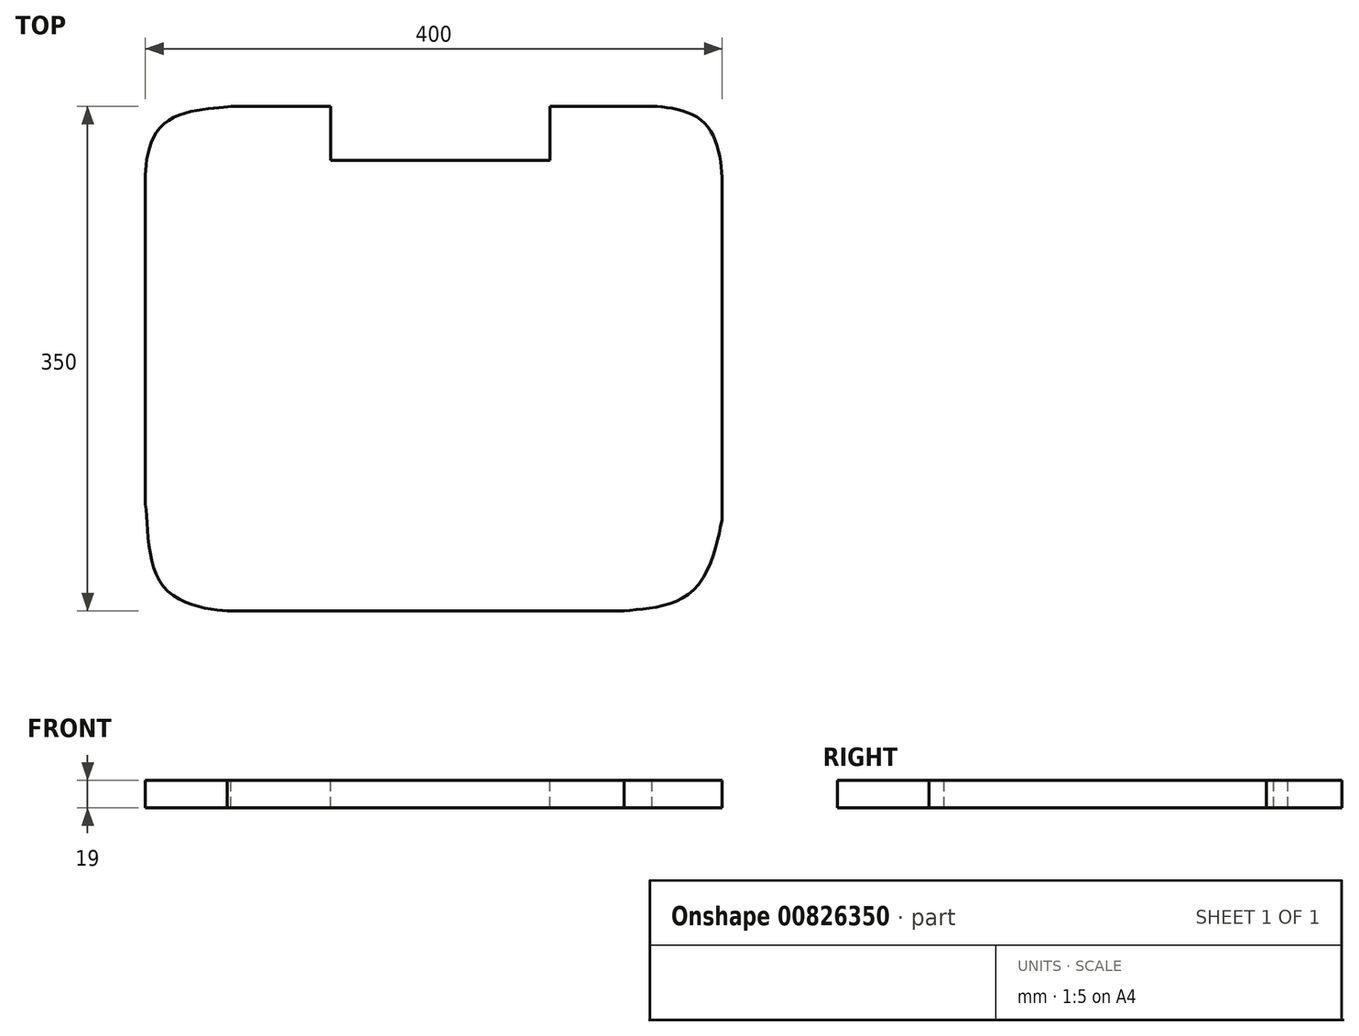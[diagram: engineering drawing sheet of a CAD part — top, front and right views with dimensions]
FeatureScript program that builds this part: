
annotation { "Feature Type Name" : "Feature", "Feature Type Description" : "" }
export const myFeature = defineFeature(function(context is Context, id is Id, definition is map)
    precondition{}
    {
        {
            var Q0;
            Q0=qCreatedBy(makeId("Top.planeOp"),FACE);
            var sketch = newSketch(context, id + "F0", { "sketchPlane" : qUnion([Q0])});
            skLineSegment(sketch, "E0.bottom", {"start": v(-200, 175) * mm, "end": v(200, 175) * mm});
            skLineSegment(sketch, "E0.top", {"start": v(-200, -175) * mm, "end": v(200, -175) * mm});
            skLineSegment(sketch, "E0.left", {"start": v(-200, 175) * mm, "end": v(-200, -175) * mm});
            skLineSegment(sketch, "E0.right", {"start": v(200, 175) * mm, "end": v(200, -175) * mm});
            skPoint(sketch, "E0.middle", {"position": v(0, 0) * mm});
            skSolve(sketch);
        }
        {
            var Q0;
            Q0=makeQuery(id+"F0.imprint","IMPRINT",FACE,{"disambiguationData":[TD([[makeQuery(id+"F0.imprint","IMPRINT",EDGE,{"derivedFrom":sQuery(id+"F0.wireOp",EDGE,"E0.bottom")}),-1.0]])]});
            extrude(context, id + "F1", {"entities" : qUnion([Q0]), "depth" : 19 * mm, "offsetDistance" : 25 * mm});
        }
        {
            var Q0;
            Q0=makeQuery(id+"F1.opExtrude","CAP_FACE",FACE,{"disambiguationData":[OSD([sQuery(id+"F0.wireOp",EDGE,"E0.bottom"),sQuery(id+"F0.wireOp",EDGE,"E0.top"),sQuery(id+"F0.wireOp",EDGE,"E0.left"),sQuery(id+"F0.wireOp",EDGE,"E0.right")])],"isStart":false});
            var sketch = newSketch(context, id + "F2", { "sketchPlane" : qUnion([Q0])});
            skFitSpline(sketch, "E1", {"points": [v(135.87, 175) * mm, v(187.94, 163.16) * mm, v(200, 110.13) * mm], "startDerivative": vector(58.12, 0) * mm, "endDerivative": vector(0, -51.3) * mm});
            skSolve(sketch);
        }
        {
            var Q0;
            {var subQ0=sQuery(id+"F2.wireOp",EDGE,"E1");var subQ1=makeQuery(id+"F1.opExtrude","CAP_EDGE",EDGE,{"disambiguationData":[OSD([sQuery(id+"F0.wireOp",EDGE,"E0.bottom")])],"isStart":false});var subQ2=makeQuery(id+"F2.imprint","INTERSECT",VERTEX,{"disambiguationData":[OD(1.0)],"derivedFrom":[subQ1,subQ0]});Q0=makeQuery(id+"F2.imprint","IMPRINT",FACE,{"disambiguationData":[TD([[makeQuery(id+"F2.imprint","IMPRINT",EDGE,{"disambiguationData":[TD([[subQ2,-1.0]])],"derivedFrom":subQ0}),1.0]])]});}
            extrude(context, id + "F3", {"entities" : qUnion([Q0]), "operationType" : NewBodyOperationType.REMOVE, "endBound" : BoundingType.THROUGH_ALL, "oppositeDirection" : true, "depth" : 31 * mm, "offsetDistance" : 25 * mm});
        }
        {
            var Q0;
            Q0=makeQuery(id+"F1.opExtrude","CAP_FACE",FACE,{"disambiguationData":[OSD([sQuery(id+"F0.wireOp",EDGE,"E0.bottom"),sQuery(id+"F0.wireOp",EDGE,"E0.top"),sQuery(id+"F0.wireOp",EDGE,"E0.left"),sQuery(id+"F0.wireOp",EDGE,"E0.right")])],"isStart":false});
            var sketch = newSketch(context, id + "F4", { "sketchPlane" : qUnion([Q0])});
            skFitSpline(sketch, "E2", {"points": [v(-140.76, 175) * mm, v(-189.63, 160.57) * mm, v(-200, 120.13) * mm, v(-200, 110.48) * mm], "startDerivative": vector(-65.65, -11.34) * mm, "endDerivative": vector(0, -155.76) * mm});
            skSolve(sketch);
        }
        {
            var Q0;
            {var subQ0=sQuery(id+"F4.wireOp",EDGE,"E2");var subQ1=makeQuery(id+"F1.opExtrude","CAP_EDGE",EDGE,{"disambiguationData":[OSD([sQuery(id+"F0.wireOp",EDGE,"E0.bottom")])],"isStart":false});var subQ2=makeQuery(id+"F4.imprint","INTERSECT",VERTEX,{"derivedFrom":[subQ1,subQ0]});Q0=makeQuery(id+"F4.imprint","IMPRINT",FACE,{"disambiguationData":[TD([[makeQuery(id+"F4.imprint","IMPRINT",EDGE,{"disambiguationData":[TD([[subQ2,-1.0]])],"derivedFrom":subQ0}),-1.0]])]});}
            extrude(context, id + "F5", {"entities" : qUnion([Q0]), "operationType" : NewBodyOperationType.REMOVE, "endBound" : BoundingType.THROUGH_ALL, "oppositeDirection" : true, "depth" : 25 * mm, "offsetDistance" : 25 * mm});
        }
        {
            var Q0;
            Q0=makeQuery(id+"F1.opExtrude","CAP_FACE",FACE,{"disambiguationData":[OSD([sQuery(id+"F0.wireOp",EDGE,"E0.bottom"),sQuery(id+"F0.wireOp",EDGE,"E0.top"),sQuery(id+"F0.wireOp",EDGE,"E0.left"),sQuery(id+"F0.wireOp",EDGE,"E0.right")])],"isStart":false});
            var sketch = newSketch(context, id + "F6", { "sketchPlane" : qUnion([Q0])});
            skFitSpline(sketch, "E3", {"points": [v(-200, -100.97) * mm, v(-187.15, -158.47) * mm, v(-143.25, -175) * mm, v(-132.74, -175) * mm], "startDerivative": vector(13.71, -104.16) * mm, "endDerivative": vector(42, 7.33) * mm});
            skSolve(sketch);
        }
        {
            var Q0;
            {var subQ0=sQuery(id+"F6.wireOp",EDGE,"E3");var subQ1=makeQuery(id+"F1.opExtrude","CAP_EDGE",EDGE,{"disambiguationData":[OSD([sQuery(id+"F0.wireOp",EDGE,"E0.left")])],"isStart":false});var subQ2=makeQuery(id+"F6.imprint","INTERSECT",VERTEX,{"derivedFrom":[subQ1,subQ0]});Q0=makeQuery(id+"F6.imprint","IMPRINT",FACE,{"disambiguationData":[TD([[makeQuery(id+"F6.imprint","IMPRINT",EDGE,{"disambiguationData":[TD([[subQ2,-1.0]])],"derivedFrom":subQ0}),-1.0]])]});}
            extrude(context, id + "F7", {"entities" : qUnion([Q0]), "operationType" : NewBodyOperationType.REMOVE, "endBound" : BoundingType.THROUGH_ALL, "oppositeDirection" : true, "depth" : 25 * mm, "offsetDistance" : 25 * mm});
        }
        {
            var Q0;
            Q0=makeQuery(id+"F1.opExtrude","CAP_FACE",FACE,{"disambiguationData":[OSD([sQuery(id+"F0.wireOp",EDGE,"E0.bottom"),sQuery(id+"F0.wireOp",EDGE,"E0.top"),sQuery(id+"F0.wireOp",EDGE,"E0.left"),sQuery(id+"F0.wireOp",EDGE,"E0.right")])],"isStart":false});
            var sketch = newSketch(context, id + "F8", { "sketchPlane" : qUnion([Q0])});
            skFitSpline(sketch, "E4", {"points": [v(131.87, -175) * mm, v(183.19, -157.23) * mm, v(200, -111.48) * mm, v(200, -112.1) * mm], "startDerivative": vector(97.22, 12.45) * mm, "endDerivative": vector(-2.34, -18.2) * mm});
            skSolve(sketch);
        }
        {
            var Q0;
            {var subQ0=sQuery(id+"F8.wireOp",EDGE,"E4");var subQ1=makeQuery(id+"F1.opExtrude","CAP_EDGE",EDGE,{"disambiguationData":[OSD([sQuery(id+"F0.wireOp",EDGE,"E0.top")])],"isStart":false});var subQ2=makeQuery(id+"F8.imprint","INTERSECT",VERTEX,{"derivedFrom":[subQ1,subQ0]});Q0=makeQuery(id+"F8.imprint","IMPRINT",FACE,{"disambiguationData":[TD([[makeQuery(id+"F8.imprint","IMPRINT",EDGE,{"disambiguationData":[TD([[subQ2,-1.0]])],"derivedFrom":subQ0}),-1.0]])]});}
            extrude(context, id + "F9", {"entities" : qUnion([Q0]), "operationType" : NewBodyOperationType.REMOVE, "endBound" : BoundingType.THROUGH_ALL, "oppositeDirection" : true, "depth" : 25 * mm, "offsetDistance" : 25 * mm});
        }
        {
            var Q0;
            Q0=makeQuery(id+"F1.opExtrude","CAP_FACE",FACE,{"disambiguationData":[OSD([sQuery(id+"F0.wireOp",EDGE,"E0.bottom"),sQuery(id+"F0.wireOp",EDGE,"E0.top"),sQuery(id+"F0.wireOp",EDGE,"E0.left"),sQuery(id+"F0.wireOp",EDGE,"E0.right")])],"isStart":false});
            var sketch = newSketch(context, id + "F10", { "sketchPlane" : qUnion([Q0])});
            skLineSegment(sketch, "E5.bottom", {"start": v(-71.4, 175) * mm, "end": v(80.63, 175) * mm});
            skLineSegment(sketch, "E5.top", {"start": v(-71.4, 137.35) * mm, "end": v(80.63, 137.35) * mm});
            skLineSegment(sketch, "E5.left", {"start": v(-71.4, 175) * mm, "end": v(-71.4, 137.35) * mm});
            skLineSegment(sketch, "E5.right", {"start": v(80.63, 175) * mm, "end": v(80.63, 137.35) * mm});
            skSolve(sketch);
        }
        {
            var Q0;
            Q0=makeQuery(id+"F10.imprint","IMPRINT",FACE,{"disambiguationData":[TD([[makeQuery(id+"F10.imprint","IMPRINT",EDGE,{"derivedFrom":sQuery(id+"F10.wireOp",EDGE,"E5.bottom")}),-1.0]])]});
            extrude(context, id + "F11", {"entities" : qUnion([Q0]), "operationType" : NewBodyOperationType.REMOVE, "endBound" : BoundingType.THROUGH_ALL, "oppositeDirection" : true, "depth" : 25 * mm, "offsetDistance" : 25 * mm});
        }
    });
